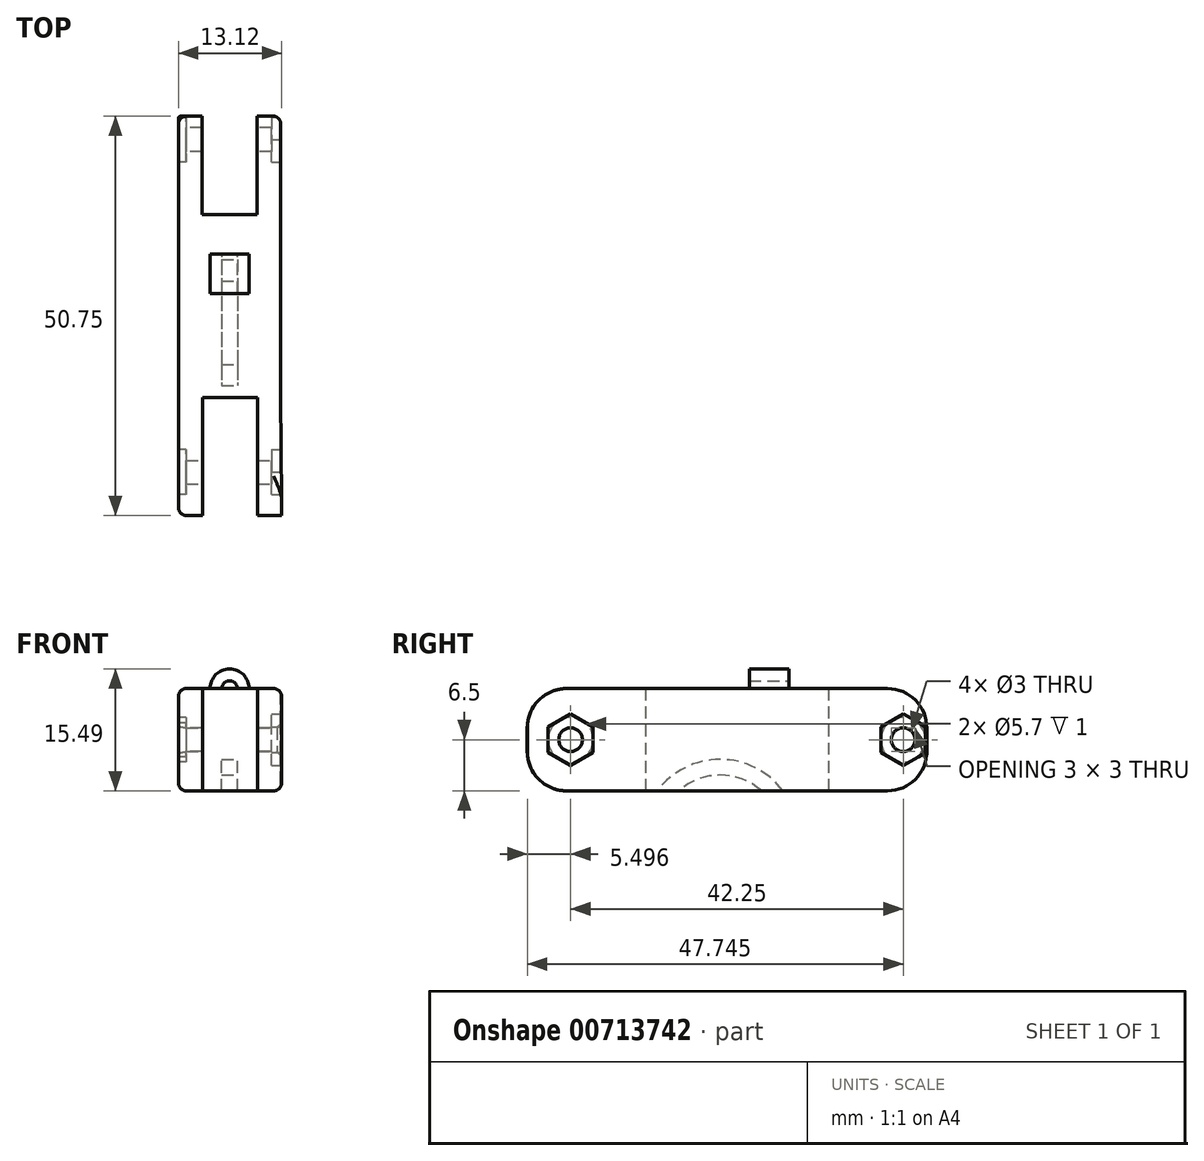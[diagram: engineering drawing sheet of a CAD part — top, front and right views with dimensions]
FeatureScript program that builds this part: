
annotation { "Feature Type Name" : "Feature", "Feature Type Description" : "" }
export const myFeature = defineFeature(function(context is Context, id is Id, definition is map)
    precondition{}
    {
        {
            var Q0;
            Q0=qCreatedBy(makeId("Top.planeOp"),FACE);
            var sketch = newSketch(context, id + "F0", { "sketchPlane" : qUnion([Q0])});
            skLineSegment(sketch, "E0.bottom", {"start": v(-6.5, 7.54) * mm, "end": v(6.5, 7.54) * mm});
            skLineSegment(sketch, "E0.top", {"start": v(-6.5, -15.71) * mm, "end": v(6.5, -15.71) * mm});
            skLineSegment(sketch, "E0.left", {"start": v(-6.5, 7.54) * mm, "end": v(-6.5, -15.71) * mm});
            skLineSegment(sketch, "E0.right", {"start": v(6.5, 7.54) * mm, "end": v(6.5, -15.71) * mm});
            skLineSegment(sketch, "E1", {"start": v(-6.5, 7.54) * mm, "end": v(-6.5, 20.04) * mm});
            skLineSegment(sketch, "E2", {"start": v(-6.5, 20.04) * mm, "end": v(-3.5, 20.04) * mm});
            skLineSegment(sketch, "E3", {"start": v(-3.5, 20.04) * mm, "end": v(-3.5, 7.54) * mm});
            skPoint(sketch, "E3.endSnap0", {"position": v(0, 7.54) * mm});
            skLineSegment(sketch, "E4", {"start": v(-3.5, 7.54) * mm, "end": v(3.5, 7.54) * mm});
            skLineSegment(sketch, "E5", {"start": v(3.5, 7.54) * mm, "end": v(3.5, 20.04) * mm});
            skLineSegment(sketch, "E6", {"start": v(3.5, 20.04) * mm, "end": v(6.5, 20.04) * mm});
            skLineSegment(sketch, "E7", {"start": v(6.5, 20.04) * mm, "end": v(6.5, 7.54) * mm});
            skLineSegment(sketch, "E8", {"start": v(-6.5, -15.71) * mm, "end": v(-6.5, -30.71) * mm});
            skLineSegment(sketch, "E9", {"start": v(-6.5, -30.71) * mm, "end": v(-3.44, -30.71) * mm});
            skLineSegment(sketch, "E10", {"start": v(-3.44, -30.71) * mm, "end": v(-3.44, -15.71) * mm});
            skLineSegment(sketch, "E11", {"start": v(-3.44, -15.71) * mm, "end": v(3.56, -15.71) * mm});
            skLineSegment(sketch, "E12", {"start": v(3.56, -15.71) * mm, "end": v(3.56, -30.71) * mm});
            skLineSegment(sketch, "E13", {"start": v(3.56, -30.71) * mm, "end": v(6.62, -30.71) * mm});
            skLineSegment(sketch, "E14", {"start": v(6.62, -30.71) * mm, "end": v(6.5, -15.71) * mm});
            skPoint(sketch, "E15", {"position": v(-6.5, -23.21) * mm});
            skPoint(sketch, "E16", {"position": v(-6.5, 13.79) * mm});
            skSolve(sketch);
        }
        {
            var Q0;
            {var subQ3=sQuery(id+"F0.wireOp",EDGE,"E0.left");Q0=makeQuery(id+"F0.imprint","IMPRINT",FACE,{"disambiguationData":[TD([[makeQuery(id+"F0.imprint","IMPRINT",EDGE,{"derivedFrom":subQ3}),1.0]])]});}
            var Q1;
            {var subQ0=sQuery(id+"F0.wireOp",EDGE,"E1");Q1=makeQuery(id+"F0.imprint","IMPRINT",FACE,{"disambiguationData":[TD([[makeQuery(id+"F0.imprint","IMPRINT",EDGE,{"derivedFrom":subQ0}),-1.0]])]});}
            var Q2;
            {var subQ2=sQuery(id+"F0.wireOp",EDGE,"E5");Q2=makeQuery(id+"F0.imprint","IMPRINT",FACE,{"disambiguationData":[TD([[makeQuery(id+"F0.imprint","IMPRINT",EDGE,{"derivedFrom":subQ2}),-1.0]])]});}
            var Q3;
            {var subQ0=sQuery(id+"F0.wireOp",EDGE,"E8");Q3=makeQuery(id+"F0.imprint","IMPRINT",FACE,{"disambiguationData":[TD([[makeQuery(id+"F0.imprint","IMPRINT",EDGE,{"derivedFrom":subQ0}),1.0]])]});}
            var Q4;
            {var subQ2=sQuery(id+"F0.wireOp",EDGE,"E12");Q4=makeQuery(id+"F0.imprint","IMPRINT",FACE,{"disambiguationData":[TD([[makeQuery(id+"F0.imprint","IMPRINT",EDGE,{"derivedFrom":subQ2}),1.0]])]});}
            extrude(context, id + "F1", {"entities" : qUnion([Q0, Q1, Q2, Q3, Q4]), "depth" : 13 * mm});
        }
        {
            var Q0;
            Q0=makeQuery(id+"F1.opExtrude","CAP_EDGE",EDGE,{"disambiguationData":[OSD([sQuery(id+"F0.wireOp",EDGE,"E13")])],"isStart":true});
            var Q1;
            Q1=makeQuery(id+"F1.opExtrude","CAP_EDGE",EDGE,{"disambiguationData":[OSD([sQuery(id+"F0.wireOp",EDGE,"E13")])],"isStart":false});
            var Q2;
            Q2=makeQuery(id+"F1.opExtrude","CAP_EDGE",EDGE,{"disambiguationData":[OSD([sQuery(id+"F0.wireOp",EDGE,"E9")])],"isStart":false});
            var Q3;
            Q3=makeQuery(id+"F1.opExtrude","CAP_EDGE",EDGE,{"disambiguationData":[OSD([sQuery(id+"F0.wireOp",EDGE,"E9")])],"isStart":true});
            var Q4;
            Q4=makeQuery(id+"F1.opExtrude","CAP_EDGE",EDGE,{"disambiguationData":[OSD([sQuery(id+"F0.wireOp",EDGE,"E2")])],"isStart":false});
            var Q5;
            Q5=makeQuery(id+"F1.opExtrude","CAP_EDGE",EDGE,{"disambiguationData":[OSD([sQuery(id+"F0.wireOp",EDGE,"E2")])],"isStart":true});
            var Q6;
            Q6=makeQuery(id+"F1.opExtrude","CAP_EDGE",EDGE,{"disambiguationData":[OSD([sQuery(id+"F0.wireOp",EDGE,"E6")])],"isStart":false});
            var Q7;
            Q7=makeQuery(id+"F1.opExtrude","CAP_EDGE",EDGE,{"disambiguationData":[OSD([sQuery(id+"F0.wireOp",EDGE,"E6")])],"isStart":true});
            fillet(context, id + "F2", {"entities" : qUnion([Q0, Q1, Q2, Q3, Q4, Q5, Q6, Q7]), "radius" : 5 * mm, "tangentPropagation" : true, "allowEdgeOverflow" : false});
        }
        {
            var Q0;
            Q0=qCreatedBy(makeId("Right.planeOp"),FACE);
            var sketch = newSketch(context, id + "F3", { "sketchPlane" : qUnion([Q0])});
            skPoint(sketch, "E17", {"position": v(20.54, 6.5) * mm});
            skPoint(sketch, "E18", {"position": v(17.04, 0.13) * mm});
            skCircle(sketch, "E19", {"center": v(17.04, 6.5) * mm, "radius": 1.5 * mm});
            skCircle(sketch, "E20.MirrorC", {"center": v(-25.21, 6.5) * mm, "radius": 1.5 * mm});
            skPoint(sketch, "E21.orphan", {"position": v(20.54, 0.13) * mm});
            skPoint(sketch, "E22.0.2.start.orphan", {"position": v(13.54, 0.13) * mm});
            skPoint(sketch, "E22.0.3.end.orphan", {"position": v(20.54, 12.87) * mm});
            skPoint(sketch, "E22.0.3.start.orphan", {"position": v(14.29, 12.87) * mm});
            skPoint(sketch, "E23", {"position": v(0, 13.07) * mm});
            skSolve(sketch);
        }
        {
            var Q0;
            Q0=makeQuery(id+"F3.imprint","IMPRINT",FACE,{"disambiguationData":[TD([[makeQuery(id+"F3.imprint","IMPRINT",EDGE,{"derivedFrom":sQuery(id+"F3.wireOp",EDGE,"E19")}),1.0]])]});
            var Q1;
            Q1=makeQuery(id+"F3.imprint","IMPRINT",FACE,{"disambiguationData":[TD([[makeQuery(id+"F3.imprint","IMPRINT",EDGE,{"derivedFrom":sQuery(id+"F3.wireOp",EDGE,"E20.MirrorC")}),-1.0]])]});
            var Q2;
            Q2=sQuery(id+"F3.wireOp",EDGE,"E19");
            extrude(context, id + "F4", {"entities" : qUnion([Q0, Q1]), "operationType" : NewBodyOperationType.REMOVE, "surfaceEntities" : qUnion([Q2]), "endBound" : BoundingType.SYMMETRIC, "depth" : 54 * mm});
        }
        {
            var Q0;
            Q0=qSketchRegion(id+"F3",true);
            extrude(context, id + "F5", {"entities" : qUnion([Q0]), "operationType" : NewBodyOperationType.REMOVE, "endBound" : BoundingType.SYMMETRIC, "oppositeDirection" : true, "depth" : 25 * mm});
        }
        {
            var Q0;
            Q0=makeQuery(id+"F1.opExtrude","SWEPT_FACE",FACE,{"disambiguationData":[OSD([sQuery(id+"F0.wireOp",EDGE,"E0.left"),sQuery(id+"F0.wireOp",EDGE,"E1"),sQuery(id+"F0.wireOp",EDGE,"E8")])]});
            var sketch = newSketch(context, id + "F6", { "sketchPlane" : qUnion([Q0])});
            skCircle(sketch, "E24", {"center": v(25.21, 6.5) * mm, "radius": 2.85 * mm});
            skCircle(sketch, "E25", {"center": v(-17.04, 6.5) * mm, "radius": 2.85 * mm});
            skSolve(sketch);
        }
        {
            var Q0;
            Q0=qSketchRegion(id+"F6",true);
            extrude(context, id + "F7", {"entities" : qUnion([Q0]), "operationType" : NewBodyOperationType.REMOVE, "oppositeDirection" : true, "depth" : 1 * mm});
        }
        {
            var Q0;
            Q0=makeQuery(id+"F1.opExtrude","SWEPT_FACE",FACE,{"disambiguationData":[OSD([sQuery(id+"F0.wireOp",EDGE,"E0.right"),sQuery(id+"F0.wireOp",EDGE,"E7"),sQuery(id+"F0.wireOp",EDGE,"E14")])]});
            var sketch = newSketch(context, id + "F8", { "sketchPlane" : qUnion([Q0])});
            skCircle(sketch, "E26.cCircle", {"center": v(-25.21, 6.5) * mm, "radius": 2.85 * mm, "construction": true});
            skLineSegment(sketch, "E26.0", {"start": v(-28.06, 8.15) * mm, "end": v(-25.21, 9.8) * mm});
            skLineSegment(sketch, "E26.1", {"start": v(-25.21, 9.8) * mm, "end": v(-22.36, 8.15) * mm});
            skLineSegment(sketch, "E26.2", {"start": v(-22.36, 8.15) * mm, "end": v(-22.36, 4.85) * mm});
            skLineSegment(sketch, "E26.3", {"start": v(-22.36, 4.85) * mm, "end": v(-25.21, 3.2) * mm});
            skLineSegment(sketch, "E26.4", {"start": v(-25.21, 3.2) * mm, "end": v(-28.06, 4.85) * mm});
            skLineSegment(sketch, "E26.5", {"start": v(-28.06, 4.85) * mm, "end": v(-28.06, 8.15) * mm});
            skPoint(sketch, "E26.0.midPoint", {"position": v(-26.64, 8.97) * mm});
            skCircle(sketch, "E27.cCircle", {"center": v(17.04, 6.5) * mm, "radius": 2.85 * mm, "construction": true});
            skLineSegment(sketch, "E27.0", {"start": v(14.19, 8.15) * mm, "end": v(17.04, 9.8) * mm});
            skLineSegment(sketch, "E27.1", {"start": v(17.04, 9.8) * mm, "end": v(19.89, 8.15) * mm});
            skLineSegment(sketch, "E27.2", {"start": v(19.89, 8.15) * mm, "end": v(19.89, 4.85) * mm});
            skLineSegment(sketch, "E27.3", {"start": v(19.89, 4.85) * mm, "end": v(17.04, 3.2) * mm});
            skLineSegment(sketch, "E27.4", {"start": v(17.04, 3.2) * mm, "end": v(14.19, 4.85) * mm});
            skLineSegment(sketch, "E27.5", {"start": v(14.19, 4.85) * mm, "end": v(14.19, 8.15) * mm});
            skPoint(sketch, "E27.0.midPoint", {"position": v(15.61, 8.97) * mm});
            skSolve(sketch);
        }
        {
            var Q0;
            Q0=makeQuery(id+"F8.imprint","IMPRINT",FACE,{"disambiguationData":[TD([[makeQuery(id+"F8.imprint","IMPRINT",EDGE,{"derivedFrom":sQuery(id+"F8.wireOp",EDGE,"E26.0")}),-1.0]])]});
            var Q1;
            Q1=makeQuery(id+"F8.imprint","IMPRINT",FACE,{"disambiguationData":[TD([[makeQuery(id+"F8.imprint","IMPRINT",EDGE,{"derivedFrom":sQuery(id+"F8.wireOp",EDGE,"E27.0")}),-1.0]])]});
            extrude(context, id + "F9", {"entities" : qUnion([Q0, Q1]), "operationType" : NewBodyOperationType.REMOVE, "oppositeDirection" : true, "depth" : 1.2 * mm});
        }
        {
            var Q0;
            Q0=qSketchRegion(id+"F6",true);
            extrude(context, id + "F10", {"entities" : qUnion([Q0]), "operationType" : NewBodyOperationType.REMOVE, "oppositeDirection" : true, "depth" : 1 * mm});
        }
        {
            var Q0;
            Q0=qSketchRegion(id+"F8",true);
            extrude(context, id + "F11", {"entities" : qUnion([Q0]), "operationType" : NewBodyOperationType.REMOVE, "oppositeDirection" : true, "depth" : 1 * mm});
        }
        {
            var Q0;
            Q0=makeQuery(id+"F1.opExtrude","CAP_EDGE",EDGE,{"disambiguationData":[OSD([sQuery(id+"F0.wireOp",EDGE,"E0.left"),sQuery(id+"F0.wireOp",EDGE,"E1"),sQuery(id+"F0.wireOp",EDGE,"E8")])],"isStart":true});
            var Q1;
            Q1=makeQuery(id+"F1.opExtrude","CAP_EDGE",EDGE,{"disambiguationData":[OSD([sQuery(id+"F0.wireOp",EDGE,"E0.right"),sQuery(id+"F0.wireOp",EDGE,"E7"),sQuery(id+"F0.wireOp",EDGE,"E14")])],"isStart":true});
            fillet(context, id + "F12", {"entities" : qUnion([Q0, Q1]), "radius" : 1 * mm, "tangentPropagation" : true, "allowEdgeOverflow" : false});
        }
        {
            var Q0;
            Q0=qCreatedBy(makeId("Front.planeOp"),FACE);
            var sketch = newSketch(context, id + "F13", { "sketchPlane" : qUnion([Q0])});
            skArc(sketch, "E28", {"start": v(0.99, 13) * mm, "mid": v(0, 13.99) * mm, "end": v(-0.99, 13) * mm});
            skArc(sketch, "E29", {"start": v(2.49, 13) * mm, "mid": v(0, 15.49) * mm, "end": v(-2.49, 13) * mm});
            skLineSegment(sketch, "E30", {"start": v(-2.49, 13) * mm, "end": v(-0.99, 13) * mm});
            skLineSegment(sketch, "E31", {"start": v(0.99, 13) * mm, "end": v(2.49, 13) * mm});
            skArc(sketch, "E32", {"start": v(-2.49, 0) * mm, "mid": v(0, -4.1) * mm, "end": v(2.49, 0) * mm});
            skArc(sketch, "E33", {"start": v(-0.99, 0) * mm, "mid": v(0, -0.98) * mm, "end": v(0.99, 0) * mm});
            skLineSegment(sketch, "E34", {"start": v(0.99, 0) * mm, "end": v(2.49, 0) * mm});
            skLineSegment(sketch, "E35", {"start": v(-0.99, 0) * mm, "end": v(-2.49, 0) * mm});
            skSolve(sketch);
        }
        {
            var Q0;
            Q0=makeQuery(id+"F13.imprint","IMPRINT",FACE,{"disambiguationData":[TD([[makeQuery(id+"F13.imprint","IMPRINT",EDGE,{"derivedFrom":sQuery(id+"F13.wireOp",EDGE,"E28")}),-1.0]])]});
            var Q1;
            Q1=makeQuery(id+"F13.imprint","IMPRINT",FACE,{"disambiguationData":[TD([[makeQuery(id+"F13.imprint","IMPRINT",EDGE,{"derivedFrom":sQuery(id+"F13.wireOp",EDGE,"E32")}),1.0]])]});
            extrude(context, id + "F14", {"entities" : qUnion([Q0, Q1]), "operationType" : NewBodyOperationType.ADD, "endBound" : BoundingType.SYMMETRIC, "depth" : 5 * mm});
        }
        {
            var Q0;
            Q0=makeQuery(id+"F8.imprint","IMPRINT",FACE,{"disambiguationData":[TD([[makeQuery(id+"F8.imprint","IMPRINT",EDGE,{"derivedFrom":sQuery(id+"F8.wireOp",EDGE,"E26.0")}),-1.0]])]});
            extrude(context, id + "F15", {"entities" : qUnion([Q0]), "operationType" : NewBodyOperationType.REMOVE, "depth" : 1.2 * mm});
        }
        {
            var Q0;
            Q0=makeQuery(id+"F14.opExtrude","CAP_FACE",FACE,{"disambiguationData":[OSD([sQuery(id+"F13.wireOp",EDGE,"E32"),sQuery(id+"F13.wireOp",EDGE,"E33"),sQuery(id+"F13.wireOp",EDGE,"E34"),sQuery(id+"F13.wireOp",EDGE,"E35")])],"isStart":true});
            var sketch = newSketch(context, id + "F16", { "sketchPlane" : qUnion([Q0])});
            skArc(sketch, "E36.0", {"start": v(2.49, 0) * mm, "mid": v(0, -4.1) * mm, "end": v(-2.49, 0) * mm});
            skArc(sketch, "E37.0.0", {"start": v(0.99, 0) * mm, "mid": v(0, -0.98) * mm, "end": v(-0.99, 0) * mm});
            skLineSegment(sketch, "E37.0.1", {"start": v(-0.99, 0) * mm, "end": v(-2.49, 0) * mm});
            skArc(sketch, "E37.0.2", {"start": v(-2.49, 0) * mm, "mid": v(0, -4.1) * mm, "end": v(2.49, 0) * mm});
            skLineSegment(sketch, "E37.0.3", {"start": v(2.49, 0) * mm, "end": v(0.99, 0) * mm});
            skSolve(sketch);
        }
        {
            var Q0;
            Q0=makeQuery(id+"F16.imprint","IMPRINT",FACE,{"disambiguationData":[TD([[makeQuery(id+"F16.imprint","IMPRINT",EDGE,{"derivedFrom":sQuery(id+"F16.wireOp",EDGE,"E37.0.0")}),1.0]])]});
            extrude(context, id + "F17", {"entities" : qUnion([Q0]), "operationType" : NewBodyOperationType.REMOVE, "endBound" : BoundingType.THROUGH_ALL, "oppositeDirection" : true, "depth" : 25 * mm});
        }
        {
            var Q0;
            Q0=qCreatedBy(makeId("Right.planeOp"),FACE);
            var sketch = newSketch(context, id + "F18", { "sketchPlane" : qUnion([Q0])});
            skArc(sketch, "E38", {"start": v(1.78, 0) * mm, "mid": v(-6.22, 4) * mm, "end": v(-14.22, 0) * mm});
            skArc(sketch, "E39", {"start": v(-0.93, 0) * mm, "mid": v(-6.22, 2) * mm, "end": v(-11.51, 0) * mm});
            skLineSegment(sketch, "E40", {"start": v(1.78, 0) * mm, "end": v(-0.93, 0) * mm});
            skLineSegment(sketch, "E41.trimOffspring", {"start": v(-11.51, 0) * mm, "end": v(-14.22, 0) * mm});
            skPoint(sketch, "E42.orphan", {"position": v(7.54, 0) * mm});
            skPoint(sketch, "E43.orphan", {"position": v(-15.71, 0) * mm});
            skSolve(sketch);
        }
        {
            var Q0;
            Q0=qSketchRegion(id+"F18",true);
            extrude(context, id + "F19", {"entities" : qUnion([Q0]), "operationType" : NewBodyOperationType.REMOVE, "endBound" : BoundingType.SYMMETRIC, "oppositeDirection" : true, "depth" : 2 * mm});
        }
    });
